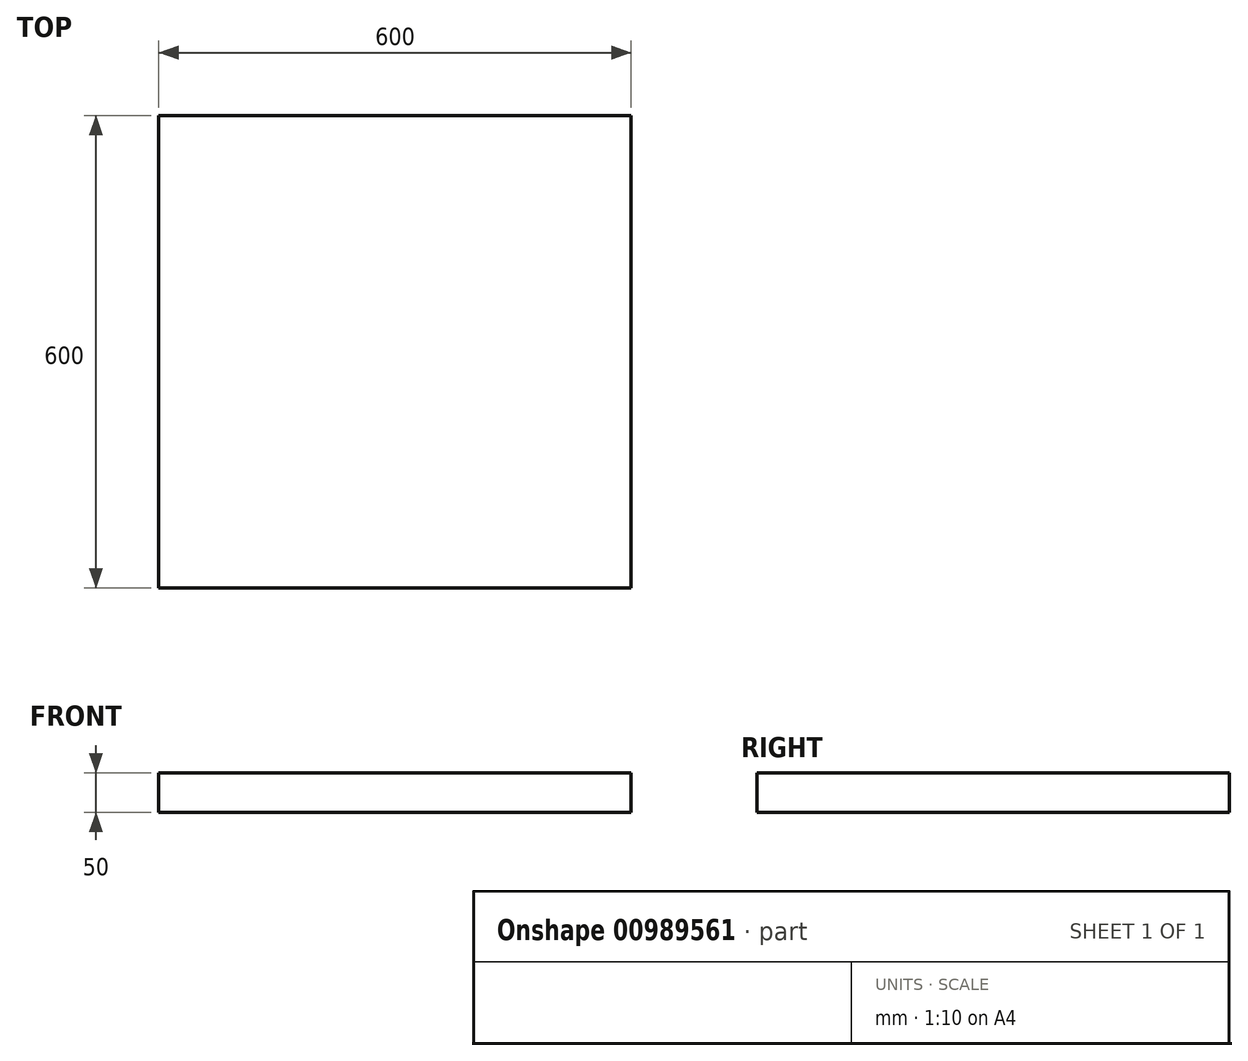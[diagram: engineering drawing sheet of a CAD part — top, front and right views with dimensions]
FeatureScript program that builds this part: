
annotation { "Feature Type Name" : "Feature", "Feature Type Description" : "" }
export const myFeature = defineFeature(function(context is Context, id is Id, definition is map)
    precondition{}
    {
        {
            var Q0;
            Q0=qCreatedBy(makeId("Top.planeOp"),FACE);
            var sketch = newSketch(context, id + "F0", { "sketchPlane" : qUnion([Q0])});
            skLineSegment(sketch, "E0.bottom", {"start": v(-300, 300) * mm, "end": v(300, 300) * mm});
            skLineSegment(sketch, "E0.top", {"start": v(-300, -300) * mm, "end": v(300, -300) * mm});
            skLineSegment(sketch, "E0.left", {"start": v(-300, 300) * mm, "end": v(-300, -300) * mm});
            skLineSegment(sketch, "E0.right", {"start": v(300, 300) * mm, "end": v(300, -300) * mm});
            skSolve(sketch);
        }
        {
            var Q0;
            Q0 = qSketchRegion(id + "F0", true);
            extrude(context, id + "F1", {"entities" : qUnion([Q0]), "depth" : 50 * mm, "offsetDistance" : 25 * mm});
        }
    });
